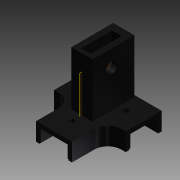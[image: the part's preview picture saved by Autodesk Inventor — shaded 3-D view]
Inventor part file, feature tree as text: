
AUTODESK INVENTOR PART (.ipt)
format: ipt  version: 2015 (Build 190159000, 159)  size: 231,424 bytes
history: native  units: in
note: dims shown in document units (in); Inventor stores cm internally (conversion verified against a paired STEP export)
features: extrude x12, sketch x12, other x3, plane x3, projected_geometry x3, split x1, fillet x1, reference x1
ambient origin geometry x8: Origin, YZ Plane, XZ Plane, XY Plane, X Axis, Y Axis, Z Axis, Center Point
bodies: Solid1 (feature_tree)
feature tree (36):
  extrude  "Extrusion1"  Depth=1.0in
  extrude  "Extrusion2"  Depth=0.5in TaperAngle=0.0deg
  extrude  "Extrusion3"  Depth=0.75in
  extrude  "Extrusion4"  Depth=1.75in TaperAngle=0.0deg
  extrude  "Extrusion5"  Depth=0.75in
  split  "Split1"
  other  "Lip1"
  other  "Lip2"
  other  "Lip3"
  extrude  "Extrusion6"  Depth=0.141in
  fillet  "Fillet1"  Radius=1.0in
  extrude  "Extrusion7"  Depth=1.0in TaperAngle=0.0deg
  plane  "Work Plane1"
  sketch  "Sketch9"  dims[d22=0.03in d23=0.03in d24=0.0in d25=0.0in d26=0.0in d27=0.0in]
  plane  "Work Plane2"
  extrude  "Extrusion8"  TaperAngle=0.0deg  [1 undecoded]
  sketch  "Sketch10"  dims[d28=0.03in d29=0.03in d30=0.0in d31=0.0in d32=0.0in d33=0.0in d34=0.141in d35=1.0in d36=0.0in]
  plane  "Work Plane3"
  extrude  "Extrusion9"  Depth=0.5in TaperAngle=0.0deg
  extrude  "Extrusion10"  Depth=0.5276in
  extrude  "Extrusion11"  Depth=0.5in TaperAngle=0.0deg
  extrude  "Extrusion12"  Depth=0.5in TaperAngle=0.0deg
  sketch  "Sketch1"  dims[d0=1.0in d1=1.0in]
  sketch  "Sketch2"  dims[d2=2.0in d3=0.0in d4=0.5in d5=0.0in]
  sketch  "Sketch4"  dims[d6=0.5in d7=0.0in d8=0.75in]
  sketch  "Sketch5"  dims[d9=0.75in d10=1.75in d11=0.0in]
  sketch  "Sketch6"  dims[d12=0.75in d13=0.75in]
  sketch  "Sketch7"  dims[d14=1.75in d15=0.0in]
  sketch  "Sketch8"  dims[d16=0.03in d17=0.03in d18=0.0in d19=0.0in d20=0.0in d21=0.0in]
  projected_geometry  "Projected Loop1"
  reference  "Reference2"
  sketch  "Sketch11"  dims[d37=0.375in d38=1.0in d39=0.0in]
  projected_geometry  "Projected Loop2"
  sketch  "Sketch12"  dims[d40=-0.2964in d41=0.0in d42=0.0in]
  sketch  "Sketch13"  dims[d43=1.5625in d44=0.0in d45=0.5in d46=0.0in d47=0.5276in d48=0.5in d49=0.0in d50=0.5in d51=0.0in]
  projected_geometry  "Projected Loop3"
note: 1 required parameter value undecoded (feature->parameter linkage not recoverable at this tier; creation-order binding heuristic only, values carry confidence <= 0.55)
